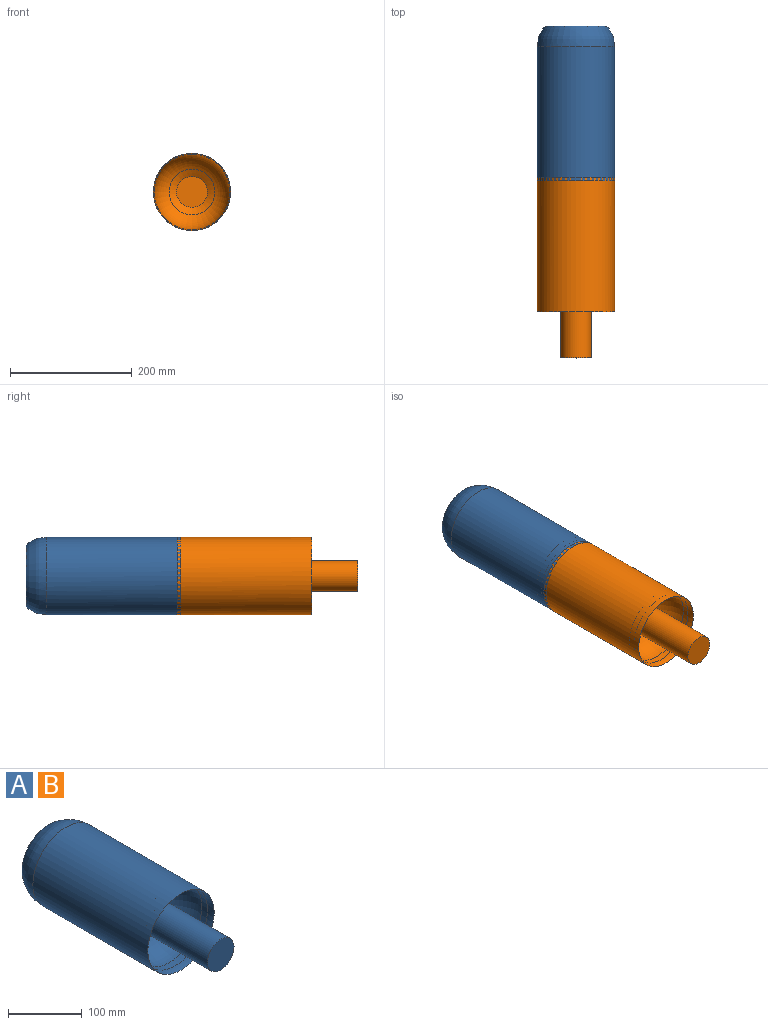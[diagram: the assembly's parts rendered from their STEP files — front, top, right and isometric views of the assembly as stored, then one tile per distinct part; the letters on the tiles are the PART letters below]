
ASSEMBLY  parts=2 mates=1
PART A: 12 faces, bbox 166.6x330.2x166.6 mm
  f0: cylinder r=25.4mm len=152.4mm, axis (0,1,0), area 24322mm2, adj f2,f11
  f1: cylinder r=63.5mm len=220.4mm, axis (0,1,0), area 87935.3mm2, adj f4,f8
  f2: plane 101.6x101.6mm, normal (0,1,0), area 6080.5mm2, adj f0,f3
  f3: cylinder r=50.8mm len=101.6mm, axis (0,1,0), area 8107.3mm2, adj f2,f4
  f4: torus R=12.7mm, axis (0,1,0), area 13654.7mm2, adj f1,f3
  f5: cone r=0mm half-angle=59deg, axis (0,-1,0), area 2815.3mm2, adj f7,f10
  f6: cylinder r=62.23mm len=124.46mm, axis (0,-1,0), area 4211.4mm2, adj f7,f8
  f7: torus R=11.43mm, axis (0,-1,0), area 17655.5mm2, adj f5,f6
  f8: torus R=113.03mm, axis (0,-1,0), area 4481.1mm2, adj f1,f6
  f9: plane 50.8x50.8mm, normal (0,-1,0), area 2026.8mm2, adj f10
  f10: cylinder r=25.4mm len=149.13mm, axis (0,1,0), area 23800mm2, adj f5,f9
  f11: plane 50.8x50.8mm, normal (0,1,0), area 2026.8mm2, adj f0
PART B: same geometry as A
PLACE A t=(-126.34,280.47,-40.67)mm
PLACE B t=(-126.34,65.05,-40.67)mm fixed
MATE slider A.f0 <-> B.f1  axis (0,1,0) through (-126.34,-49.73,-40.67)mm
